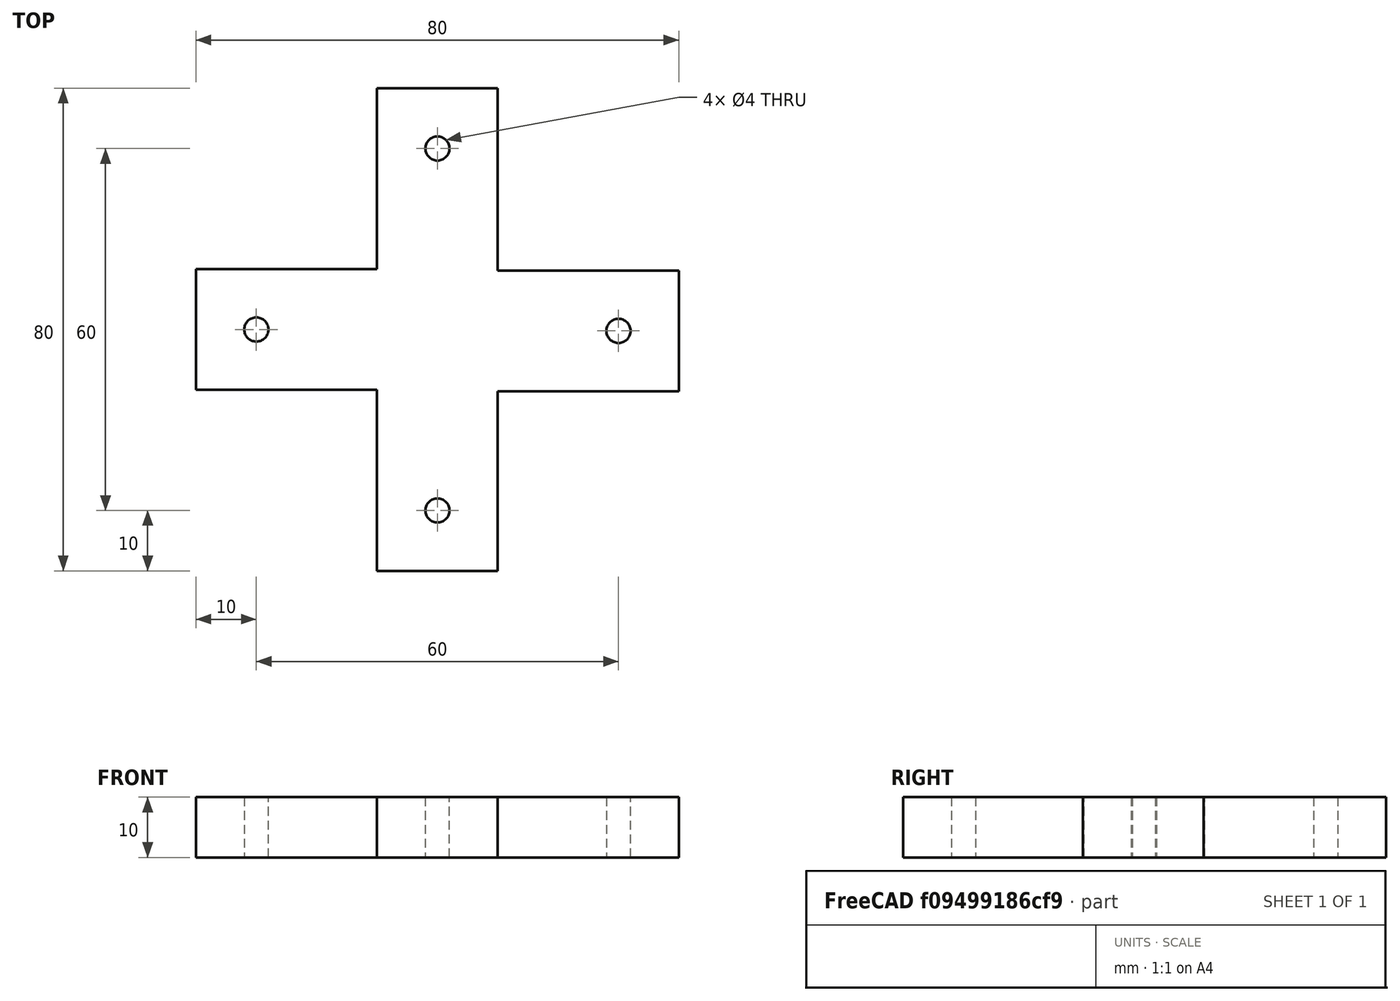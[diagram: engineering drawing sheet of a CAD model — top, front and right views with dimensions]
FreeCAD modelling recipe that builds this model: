
FCSTD DOCUMENT  (FreeCAD 0.21R33694 (Git))
Label: OJT1_T19R02_creu
License: All rights reserved
LicenseURL: http://en.wikipedia.org/wiki/All_rights_reserved
objects: Sketcher::SketchObject×1, PartDesign::Pad×1, PartDesign::Body×1
note: 4 computed .brp shape members not serialized (recipe doc carries the construction recipe); baked Part::Feature solids carry a one-line shape summary decoded from their .brp

FEATURE [Sketcher::SketchObject] Sketch
  FullyConstrained = false
  MapMode = 5
  Support = -> [XY_Plane]
  sketch-geometry (16):
    g0: LineSegment StartX=-20 StartY=40 StartZ=0 EndX=-20 EndY=10 EndZ=0
    g1: LineSegment StartX=-20 StartY=10 StartZ=0 EndX=-50 EndY=10 EndZ=0
    g2: LineSegment StartX=-50 StartY=10 StartZ=0 EndX=-50 EndY=-10 EndZ=0
    g3: LineSegment StartX=-50 StartY=-10 StartZ=0 EndX=-20 EndY=-10 EndZ=0
    g4: LineSegment StartX=-20 StartY=-10 StartZ=0 EndX=-20 EndY=-40 EndZ=0
    g5: LineSegment StartX=-20 StartY=-40 StartZ=0 EndX=0 EndY=-40 EndZ=0
    g6: LineSegment StartX=0 StartY=-40 StartZ=0 EndX=0 EndY=-10.2323 EndZ=0
    g7: LineSegment StartX=0 StartY=-10.2323 StartZ=0 EndX=30 EndY=-10.2323 EndZ=0
    g8: LineSegment StartX=30 StartY=-10.2323 StartZ=0 EndX=30 EndY=9.76768 EndZ=0
    g9: LineSegment StartX=30 StartY=9.76768 StartZ=0 EndX=0 EndY=9.76768 EndZ=0
    g10: LineSegment StartX=0 StartY=9.76768 StartZ=0 EndX=0 EndY=40 EndZ=0
    g11: LineSegment StartX=-20 StartY=40 StartZ=0 EndX=0 EndY=40 EndZ=0
    g12: Circle CenterX=-10 CenterY=30 CenterZ=0 NormalX=0 NormalY=0 NormalZ=1 AngleXU=0 Radius=2
    g13: Circle CenterX=-40 CenterY=0 CenterZ=0 NormalX=0 NormalY=0 NormalZ=1 AngleXU=0 Radius=2
    g14: Circle CenterX=-10 CenterY=-30 CenterZ=0 NormalX=0 NormalY=0 NormalZ=1 AngleXU=0 Radius=2
    g15: Circle CenterX=20 CenterY=-0.232319 CenterZ=0 NormalX=0 NormalY=0 NormalZ=1 AngleXU=0 Radius=2
  constraints (43):
    c: Vertical(g0)
    c: Coincident(g0,g1)
    c: Horizontal(g1)
    c: Coincident(g1,g2)
    c: Vertical(g2)
    c: Coincident(g2,g3)
    c: Horizontal(g3)
    c: Coincident(g3,g4)
    c: Vertical(g4)
    c: Coincident(g4,g5)
    c: PointOnObject(g5,g-2)
    c: Horizontal(g5)
    c: Coincident(g5,g6)
    c: PointOnObject(g6,g-2)
    c: Horizontal(g7)
    c: Vertical(g8)
    c: PointOnObject(g9,g-2)
    c: Horizontal(g9)
    c: PointOnObject(g10,g-2)
    c: Coincident(g0,g11)
    c: Coincident(g11,g10)
    c: Horizontal(g11)
    c: DistanceX(g11,g11) = 20
    c: DistanceY(g2,g2) = 20
    c: DistanceX(g1,g1) = 30
    c: DistanceX(g9,g9) = 30
    c: DistanceY(g4,g4) = 30
    c: DistanceY(g0,g0) = 30
    c: DistanceX(g5,g5) = 20
    c: DistanceY(g8,g8) = 20
    c: PointOnObject(g13,g-1)
    c: Diameter(g13) = 4
    c: Diameter(g12) = 4
    c: Diameter(g15) = 4
    c: Diameter(g14) = 4
    c: DistanceX(g15,g8) = 10
    c: DistanceY(g15,g8) = 10
    c: DistanceY(g13,g1) = 10
    c: DistanceY(g12,g0) = 10
    c: DistanceY(g4,g14) = 10
    c: DistanceX(g0,g12) = 10
    c: DistanceX(g1,g13) = 10
    c: DistanceX(g14,g5) = 10
FEATURE [PartDesign::Pad] Pad
  Direction = (0,0,1)
  Length = 10
  Length2 = 10
  Profile = -> Sketch
  ReferenceAxis = -> Sketch [N_Axis]
  Type = 0
FEATURE [PartDesign::Body] Body
  Group = -> [Sketch,Pad]
  Origin = -> Origin
  Tip = -> Pad
